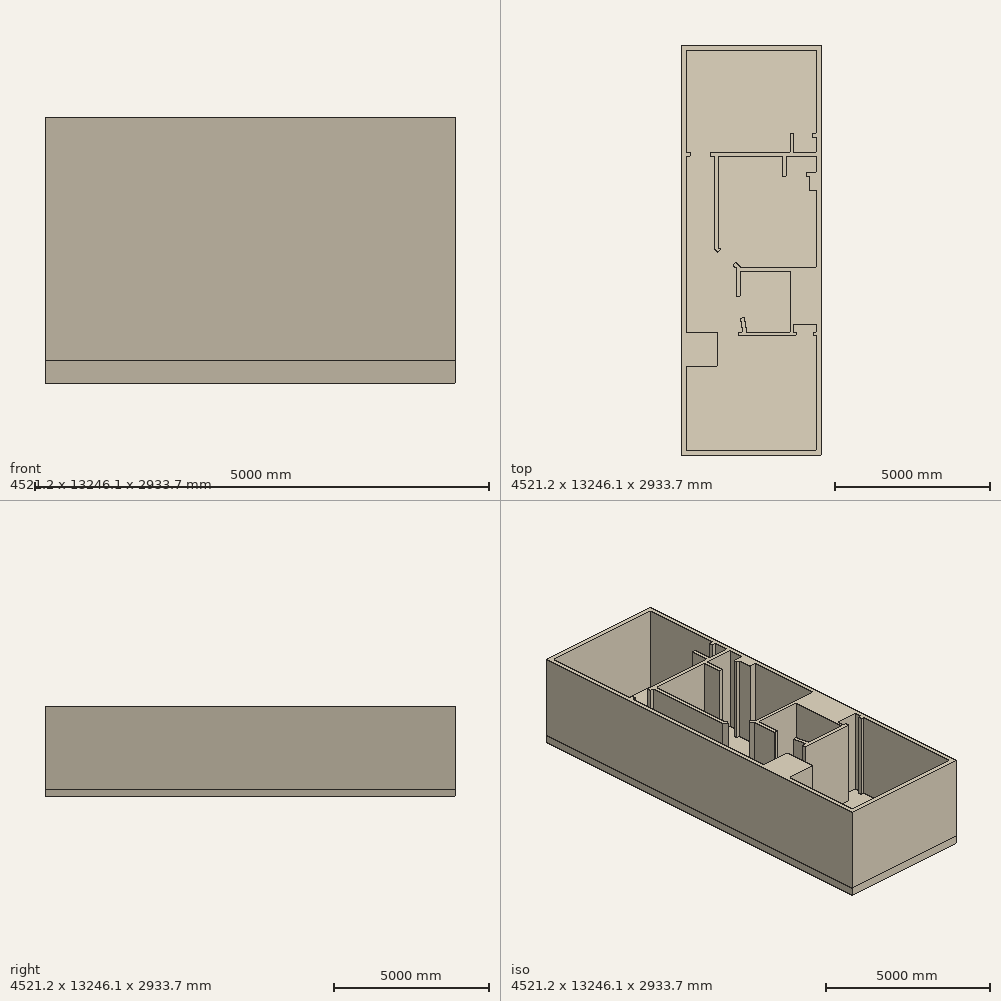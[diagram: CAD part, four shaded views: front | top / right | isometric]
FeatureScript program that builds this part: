
annotation { "Feature Type Name" : "Feature", "Feature Type Description" : "" }
export const myFeature = defineFeature(function(context is Context, id is Id, definition is map)
    precondition{}
    {
        {
            var Q0;
            Q0=qCreatedBy(makeId("Top.planeOp"),FACE);
            cPlane(context, id + "F0", {"entities" : qUnion([Q0]), "cplaneType" : CPlaneType.OFFSET, "offset" : 2933.7 * mm, "width" : 152.4 * mm, "height" : 152.4 * mm});
        }
        {
            var Q0;
            Q0=qCreatedBy(id+"F0.planeOp",FACE);
            var sketch = newSketch(context, id + "F1", { "sketchPlane" : qUnion([Q0])});
            skLineSegment(sketch, "E0.bottom", {"start": v(0, 0) * mm, "end": v(4216.4, 0) * mm});
            skLineSegment(sketch, "E0.top", {"start": v(0, 12941.3) * mm, "end": v(4216.4, 12941.3) * mm});
            skLineSegment(sketch, "E0.right", {"start": v(4216.4, 0) * mm, "end": v(4216.4, 3708.4) * mm});
            skLineSegment(sketch, "E1.0", {"start": v(-152.4, 13093.7) * mm, "end": v(4368.8, 13093.7) * mm});
            skLineSegment(sketch, "E1.1", {"start": v(-152.4, -152.4) * mm, "end": v(-152.4, 13093.7) * mm});
            skLineSegment(sketch, "E1.2", {"start": v(-152.4, -152.4) * mm, "end": v(4368.8, -152.4) * mm});
            skLineSegment(sketch, "E1.3", {"start": v(4368.8, -152.4) * mm, "end": v(4368.8, 13093.7) * mm});
            skLineSegment(sketch, "E2.trimOffspring", {"start": v(4216.4, 5918.2) * mm, "end": v(4216.4, 8394.7) * mm});
            skLineSegment(sketch, "E3.trimOffspring", {"start": v(4216.4, 9626.6) * mm, "end": v(4216.4, 10134.6) * mm});
            skLineSegment(sketch, "E4.trimOffspring", {"start": v(0, 9626.6) * mm, "end": v(0, 12941.3) * mm});
            skLineSegment(sketch, "E5.trimOffspring", {"start": v(0, 0) * mm, "end": v(0, 2717.8) * mm});
            skLineSegment(sketch, "E6.bottom", {"start": v(0, 9626.6) * mm, "end": v(127, 9626.6) * mm});
            skLineSegment(sketch, "E6.top", {"start": v(0, 9499.6) * mm, "end": v(127, 9499.6) * mm});
            skLineSegment(sketch, "E6.right", {"start": v(127, 9626.6) * mm, "end": v(127, 9499.6) * mm});
            skLineSegment(sketch, "E7", {"start": v(901.7, 6515.1) * mm, "end": v(901.7, 9499.6) * mm});
            skLineSegment(sketch, "E8", {"start": v(901.7, 9499.6) * mm, "end": v(774.7, 9499.6) * mm});
            skLineSegment(sketch, "E9", {"start": v(774.7, 9499.6) * mm, "end": v(774.7, 9626.6) * mm});
            skLineSegment(sketch, "E10", {"start": v(774.7, 9626.6) * mm, "end": v(3352.8, 9626.6) * mm});
            skLineSegment(sketch, "E11", {"start": v(3352.8, 9626.6) * mm, "end": v(3352.8, 10261.6) * mm});
            skLineSegment(sketch, "E12", {"start": v(3352.8, 10261.6) * mm, "end": v(3479.8, 10261.6) * mm});
            skLineSegment(sketch, "E13", {"start": v(3479.8, 10261.6) * mm, "end": v(3479.8, 9626.6) * mm});
            skLineSegment(sketch, "E14", {"start": v(3479.8, 9626.6) * mm, "end": v(4216.4, 9626.6) * mm});
            skLineSegment(sketch, "E15.bottom", {"start": v(4216.4, 10134.6) * mm, "end": v(4089.4, 10134.6) * mm});
            skLineSegment(sketch, "E15.top", {"start": v(4216.4, 10261.6) * mm, "end": v(4089.4, 10261.6) * mm});
            skLineSegment(sketch, "E15.right", {"start": v(4089.4, 10134.6) * mm, "end": v(4089.4, 10261.6) * mm});
            skLineSegment(sketch, "E16.trimOffspring", {"start": v(4216.4, 10261.6) * mm, "end": v(4216.4, 12941.3) * mm});
            skLineSegment(sketch, "E17", {"start": v(901.7, 6515.1) * mm, "end": v(1026.75, 6407.3) * mm});
            skLineSegment(sketch, "E18", {"start": v(1638.3, 5880.1) * mm, "end": v(1638.3, 4991.1) * mm});
            skLineSegment(sketch, "E19.0", {"start": v(1028.7, 6573.3) * mm, "end": v(1028.7, 9499.6) * mm});
            skLineSegment(sketch, "E20", {"start": v(1028.7, 9499.6) * mm, "end": v(3111.5, 9499.6) * mm});
            skLineSegment(sketch, "E21", {"start": v(3111.5, 9499.6) * mm, "end": v(3111.5, 8864.6) * mm});
            skLineSegment(sketch, "E22", {"start": v(3111.5, 8864.6) * mm, "end": v(3238.5, 8864.6) * mm});
            skLineSegment(sketch, "E23", {"start": v(3238.5, 8864.6) * mm, "end": v(3238.5, 9499.6) * mm});
            skLineSegment(sketch, "E24", {"start": v(3238.5, 9499.6) * mm, "end": v(4216.4, 9499.6) * mm});
            skLineSegment(sketch, "E25", {"start": v(4216.4, 9499.6) * mm, "end": v(4216.4, 8978.9) * mm});
            skLineSegment(sketch, "E26", {"start": v(4216.4, 8978.9) * mm, "end": v(3873.5, 8978.9) * mm});
            skLineSegment(sketch, "E27", {"start": v(3873.5, 8978.9) * mm, "end": v(3873.5, 8864.6) * mm});
            skLineSegment(sketch, "E28", {"start": v(3873.5, 8864.6) * mm, "end": v(3975.1, 8864.6) * mm});
            skLineSegment(sketch, "E29", {"start": v(3975.1, 8864.6) * mm, "end": v(3975.1, 8394.7) * mm});
            skLineSegment(sketch, "E30", {"start": v(3975.1, 8394.7) * mm, "end": v(4216.4, 8394.7) * mm});
            skLineSegment(sketch, "E31.bottom", {"start": v(4216.4, 5918.2) * mm, "end": v(1788.6, 5918.2) * mm});
            skLineSegment(sketch, "E32.0", {"start": v(1028.7, 6573.3) * mm, "end": v(1109.67, 6503.5) * mm});
            skLineSegment(sketch, "E33", {"start": v(1026.75, 6407.3) * mm, "end": v(1109.67, 6503.5) * mm});
            skLineSegment(sketch, "E34", {"start": v(1522.87, 5979.6) * mm, "end": v(1605.8, 6075.8) * mm});
            skLineSegment(sketch, "E35.trimOffspring", {"start": v(1605.8, 6075.8) * mm, "end": v(1788.6, 5918.2) * mm});
            skLineSegment(sketch, "E36.trimOffspring", {"start": v(1522.87, 5979.6) * mm, "end": v(1638.3, 5880.1) * mm});
            skLineSegment(sketch, "E37.bottom", {"start": v(4216.4, 3708.4) * mm, "end": v(4114.8, 3708.4) * mm});
            skLineSegment(sketch, "E37.top", {"start": v(4216.4, 3835.4) * mm, "end": v(4114.8, 3835.4) * mm});
            skLineSegment(sketch, "E37.right", {"start": v(4114.8, 3708.4) * mm, "end": v(4114.8, 3835.4) * mm});
            skLineSegment(sketch, "E38", {"start": v(4216.4, 4076.7) * mm, "end": v(3454.4, 4076.7) * mm});
            skLineSegment(sketch, "E39", {"start": v(3454.4, 4076.7) * mm, "end": v(3454.4, 3835.4) * mm});
            skLineSegment(sketch, "E40", {"start": v(3454.4, 3835.4) * mm, "end": v(3556, 3835.4) * mm});
            skLineSegment(sketch, "E41", {"start": v(3556, 3835.4) * mm, "end": v(3556, 3708.4) * mm});
            skLineSegment(sketch, "E42", {"start": v(3556, 3708.4) * mm, "end": v(1676.4, 3708.4) * mm});
            skLineSegment(sketch, "E43", {"start": v(1676.4, 3708.4) * mm, "end": v(1676.4, 3835.4) * mm});
            skLineSegment(sketch, "E44", {"start": v(1676.4, 3835.4) * mm, "end": v(1827.12, 3835.4) * mm});
            skLineSegment(sketch, "E45", {"start": v(1754.64, 4279.03) * mm, "end": v(1827.12, 3835.4) * mm});
            skLineSegment(sketch, "E46", {"start": v(0, 3835.4) * mm, "end": v(1016, 3835.4) * mm});
            skLineSegment(sketch, "E47", {"start": v(1016, 3835.4) * mm, "end": v(1016, 2717.8) * mm});
            skLineSegment(sketch, "E48", {"start": v(1016, 2717.8) * mm, "end": v(0, 2717.8) * mm});
            skLineSegment(sketch, "E49.trimOffspring", {"start": v(0, 3835.4) * mm, "end": v(0, 9499.6) * mm});
            skLineSegment(sketch, "E50.trimOffspring", {"start": v(4216.4, 3835.4) * mm, "end": v(4216.4, 4076.7) * mm});
            skLineSegment(sketch, "E51.0", {"start": v(1765.3, 5791.2) * mm, "end": v(1765.3, 5001.4) * mm});
            skLineSegment(sketch, "E52.left", {"start": v(3365.5, 5791.2) * mm, "end": v(3365.5, 3835.4) * mm});
            skLineSegment(sketch, "E52.right", {"start": v(3492.5, 5791.2) * mm, "end": v(3492.5, 4203.7) * mm, "construction": true});
            skLineSegment(sketch, "E53.trimOffspring", {"start": v(3365.5, 5791.2) * mm, "end": v(1765.3, 5791.2) * mm});
            skLineSegment(sketch, "E54", {"start": v(1955.8, 3835.4) * mm, "end": v(3365.5, 3835.4) * mm});
            skLineSegment(sketch, "E55", {"start": v(1955.8, 3835.4) * mm, "end": v(1879.97, 4299.51) * mm});
            skLineSegment(sketch, "E56", {"start": v(1765.3, 5001.4) * mm, "end": v(1639.96, 4980.93) * mm});
            skLineSegment(sketch, "E57", {"start": v(1754.64, 4279.03) * mm, "end": v(1879.97, 4299.51) * mm});
            skLineSegment(sketch, "E58.trimOffspring", {"start": v(1639.96, 4980.93) * mm, "end": v(1638.3, 4991.1) * mm});
            skLineSegment(sketch, "E59", {"start": v(3492.5, 4203.7) * mm, "end": v(4216.4, 4203.7) * mm, "construction": true});
            skLineSegment(sketch, "E60.trimOffspring", {"start": v(4216.4, 5791.2) * mm, "end": v(3492.5, 5791.2) * mm, "construction": true});
            skSolve(sketch);
        }
        {
            var Q0;
            Q0=makeQuery(id+"F1.imprint","IMPRINT",FACE,{"disambiguationData":[TD([[makeQuery(id+"F1.imprint","IMPRINT",EDGE,{"derivedFrom":sQuery(id+"F1.wireOp",EDGE,"E0.bottom")}),-1.0]])]});
            var Q1;
            Q1=makeQuery(id+"F1.imprint","IMPRINT",FACE,{"disambiguationData":[TD([[makeQuery(id+"F1.imprint","IMPRINT",EDGE,{"derivedFrom":sQuery(id+"F1.wireOp",EDGE,"E0.bottom")}),1.0]])]});
            var Q2;
            Q2=makeQuery(id+"F1.imprint","IMPRINT",FACE,{"disambiguationData":[TD([[makeQuery(id+"F1.imprint","IMPRINT",EDGE,{"derivedFrom":sQuery(id+"F1.wireOp",EDGE,"41e67187-f327-4b45-bb31-bf1c19bb41f0.0")}),1.0]])]});
            extrude(context, id + "F2", {"entities" : qUnion([Q0, Q1, Q2]), "oppositeDirection" : true, "depth" : 254 * mm});
        }
        {
            var Q0;
            Q0=makeQuery(id+"F1.imprint","IMPRINT",FACE,{"disambiguationData":[TD([[makeQuery(id+"F1.imprint","IMPRINT",EDGE,{"derivedFrom":sQuery(id+"F1.wireOp",EDGE,"E0.bottom")}),-1.0]])]});
            extrude(context, id + "F3", {"entities" : qUnion([Q0]), "depth" : 2679.7 * mm});
        }
    });
